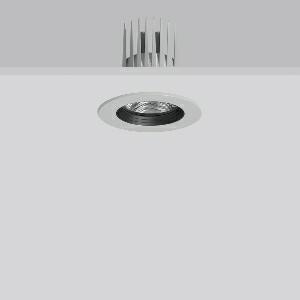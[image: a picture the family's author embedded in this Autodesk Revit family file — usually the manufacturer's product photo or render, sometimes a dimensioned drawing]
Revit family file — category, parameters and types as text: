
# Revit family: heledon_mini_e_901750_004_3_76_bbab
name_source: partatom
category: Lighting Fixtures
units: mm (PartAtom-declared; Revit-internal decimal feet)

## family parameters
Cut with Voids When Loaded = No
Host = Face
Light Source = No
Part Type = Normal
Room Calculation Point = No
Round Connector Dimension = Use Diameter
Shared = No

## types (1)
- HELEDON mini E (1 x LED Modul 935, 3800 lm, 3500)
    Apparent Load = 29 VA
    Approval mark = CE
    CIE Flux Codes = 95 99 100 100 100
    Color Rendering = 92
    Color Temperature = 3500
    Default Elevation = 1800 mm
    Description = Series: HELEDON mini
Round recessed downlight. Housing: die-cast aluminium, powder-coated. Black plastic ring and recessed LED to prevent glare from the side. Optical assembly with reflector made of MIRO-Silver with 98% total light reflection for outstanding efficiency - can be changed without tools. Best colour rendering index Ra>90. Suitable for Recessed ceiling mounting. Installation without tools thanks to spring fastening system. Including separate LED converter with connecting cable 600 mm.High quality converter without flickering and stroboscopic effect. Through-wiring box (5 pole) available as accessory. The following accessories can be mounted without use of tools: interchangeable lenses, decorative glasses, honeycomb louvre, clear and frosted diffusers, white interchangeable plastic ring. 
Colour: silver
Diameter: 124 mm
Height: 3 mm
Cut-out diameter: 114 mm
Recess height: 170 mm
Luminaire: recess height: 120 mm
Lamp: LED
Socket: without socket
Colour temperature: 3500K
Colour rendering index (CRI): 92
System power: 29 W
Rated luminous flux: 3800 lm
Luminous efficiency: 131 lm/W
Control gear: Converter, dimmable, DALI
Protection class: II
Type of protection: IP 20
    Height = 0 mm  [stored 0 ft]
    Lamp = 1 x LED Modul 935
    Lamp Light Flux = 3800 lm
    Lamp count = 1
    Length = 124 mm  [stored 0.406824 ft]
    Lifetime = 50000 h
    Luminous efficacy = 131 lm/W
    Manufacturer = RZB
    ModVariant = No
    Model = 901750.004.3.76
    Mounting Place = Ceiling
    Mounting Type = Recessed
    Number of Poles = 1
    OnlyDefault = Yes
    Power Factor = 1
    Product Name = HELEDON mini E
    Product group = Recessed downlights
    ProductGroupID = 402
    Protection Class = Protection class II
    Protection Degree = IP 20
    RLX_Detail_Level = 1
    RLX_Emergency_Light_Flux = 0 lm
    RLX_Emergency_Type = 0
    RLX_Emergency_Type_DB = No
    RlxData = <blob elided: 126089 chars, md5=329bafa4>
    Socket = socket
    Standby Power = 0 W
    System Light Flux = 3800 lm
    System Power = 29 W
    Type Comments = Product without accessories
    Type Image = 901657.004.jpg
    URL = http://relux.com
    VarID = ---
    Voltage = 230 V
    Voltage Range = 220-240 V
    Weight = 0.00 kg
    Width = 0 mm  [stored 0 ft]

note: [stored X ft] marks values corroborated as IEEE doubles in the binary element streams (Revit-internal decimal feet)

## geometry (parser evidence)
native form markers: Blend x4, Sweep x10
no freeform markers — native parametric forms only
